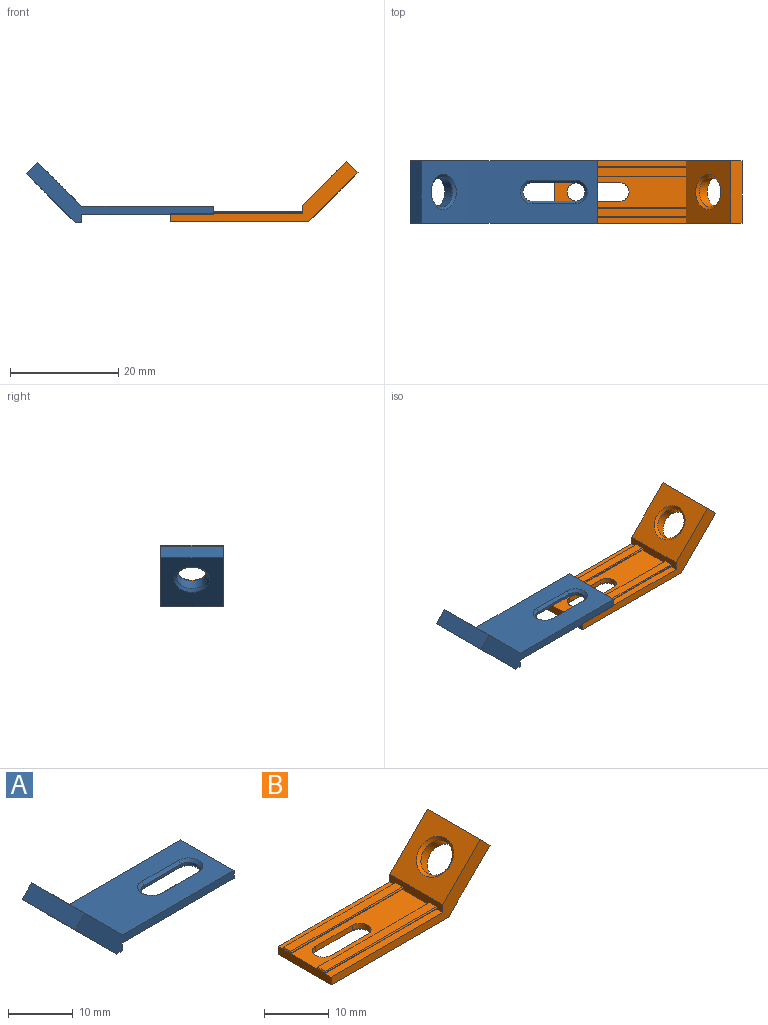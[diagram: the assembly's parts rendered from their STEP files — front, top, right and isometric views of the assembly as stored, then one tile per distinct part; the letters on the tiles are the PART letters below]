
ASSEMBLY  parts=2 mates=1
PART A: 41 faces, bbox 34.7x11.6x11.2 mm
  f0: plane 24.41x1.1mm, normal (0,0,-1), area 26.8mm2, adj f2,f5,f10,f21,f27
  f1: plane 24.41x5.6mm, normal (0,0,-1), area 86.2mm2, adj f2,f5,f16,f20,f25,f30,f31,f32
  f2: plane 11.6x1.5mm, normal (1,0,0), area 13mm2, adj f0,f1,f3,f4,f10,f11,f25,f26
  f3: plane 24.41x1.1mm, normal (0,0,-1), area 26.8mm2, adj f2,f5,f11,f17,f28
  f4: plane 24.41x11.6mm, normal (0,0,1), area 232.8mm2, adj f2,f6,f10,f11,f35,f36,f37,f38
  f5: plane 11.6x1.5mm, normal (1,0,0), area 17.4mm2, adj f0,f1,f3,f9,f10,f11,f19,f23
  f6: plane 11.6x8.2mm, normal (0.71,0,0.71), area 100.3mm2, adj f4,f7,f10,f11,f40
  f7: plane 11.6x2.12mm, normal (-0.71,0,0.71), area 34.8mm2, adj f6,f8,f10,f11
  f8: plane 11.6x9.08mm, normal (-0.71,0,-0.71), area 114.8mm2, adj f7,f9,f10,f11,f39
  f9: plane 11.6x1.24mm, normal (0,0,-1), area 14.4mm2, adj f5,f8,f10,f11
  f10: plane 34.73x11.2mm, normal (0,-1,0), area 75.1mm2, adj f0,f2,f4,f5,f6,f7,f8,f9
  f11: plane 34.73x11.2mm, normal (0,1,0), area 75.1mm2, adj f2,f3,f4,f5,f6,f7,f8,f9
  f12: plane 8x0.5mm, normal (0,1,0), area 4mm2, adj f13,f15,f31,f35
  f13: cylinder r=1.7mm len=3.4mm, axis (0,0,1), area 2.7mm2, adj f12,f14,f32,f37
  f14: plane 8x0.5mm, normal (0,-1,0), area 4mm2, adj f13,f15,f34,f38
  f15: cylinder r=1.7mm len=3.4mm, axis (0,0,1), area 2.7mm2, adj f12,f14,f33,f36
  f16: plane 24.45x0.5mm, normal (0,0.87,0.5), area 14mm2, adj f1,f18,f19,f30
  f17: plane 24.45x0.5mm, normal (0,-0.87,0.5), area 14mm2, adj f3,f18,f19,f28
  f18: plane 24.45x2.48mm, normal (0,0,-1), area 60.6mm2, adj f16,f17,f19,f29
  f19: plane 2.48x0.5mm, normal (0.87,0,0.5), area 1.3mm2, adj f5,f16,f17,f18
  f20: plane 24.45x0.5mm, normal (0,-0.87,0.5), area 14mm2, adj f1,f22,f23,f25
  f21: plane 24.45x0.5mm, normal (0,0.87,0.5), area 14mm2, adj f0,f22,f23,f27
  f22: plane 24.45x2.48mm, normal (0,0,-1), area 60.6mm2, adj f20,f21,f23,f26
  f23: plane 2.48x0.5mm, normal (0.87,0,0.5), area 1.3mm2, adj f5,f20,f21,f22
  f24: cylinder r=2.8mm len=5.6mm, axis (0.71,0,0.71), area 35.2mm2, adj f39,f40
  f25: plane 0.75x0.72mm, normal (0.71,-0.61,0.35), area 0.3mm2, adj f1,f2,f20,f26
  f26: plane 3.34x0.25mm, normal (0.71,0,-0.71), area 1mm2, adj f2,f22,f25,f27
  f27: plane 0.75x0.72mm, normal (0.71,0.61,0.35), area 0.3mm2, adj f0,f2,f21,f26
  f28: plane 0.75x0.72mm, normal (0.71,-0.61,0.35), area 0.3mm2, adj f2,f3,f17,f29
  f29: plane 3.34x0.25mm, normal (0.71,0,-0.71), area 1mm2, adj f2,f18,f28,f30
  f30: plane 0.75x0.72mm, normal (0.71,0.61,0.35), area 0.3mm2, adj f1,f2,f16,f29
  f31: plane 8x0.5mm, normal (0,0.71,-0.71), area 5.7mm2, adj f1,f12,f32,f33
  f32: cone r=2.2mm half-angle=45deg, axis (0,0,-1), area 4.3mm2, adj f1,f13,f31,f34
  f33: cone r=2.2mm half-angle=45deg, axis (0,0,-1), area 4.3mm2, adj f1,f15,f31,f34
  f34: plane 8x0.5mm, normal (0,-0.71,-0.71), area 5.7mm2, adj f1,f14,f32,f33
  f35: plane 8x0.5mm, normal (0,0.71,0.71), area 5.7mm2, adj f4,f12,f36,f37
  f36: cone r=2.2mm half-angle=45deg, axis (0,0,1), area 4.3mm2, adj f4,f15,f35,f38
  f37: cone r=2.2mm half-angle=45deg, axis (0,0,1), area 4.3mm2, adj f4,f13,f35,f38
  f38: plane 8x0.5mm, normal (0,-0.71,0.71), area 5.7mm2, adj f4,f14,f36,f37
  f39: cone r=2.8mm half-angle=45deg, axis (-0.71,0,-0.71), area 13.6mm2, adj f8,f24
  f40: cone r=2.8mm half-angle=45deg, axis (0.71,0,0.71), area 13.6mm2, adj f6,f24
PART B: 44 faces, bbox 34.9x11.6x11.2 mm
  f0: plane 24.41x6.25mm, normal (0,0,1), area 110.2mm2, adj f4,f8,f11,f12,f13,f14,f17,f19
  f1: plane 24.41x1.43mm, normal (0,0,1), area 31.7mm2, adj f4,f8,f10,f15,f24
  f2: plane 24.41x1.43mm, normal (0,0,1), area 31.7mm2, adj f4,f8,f9,f21,f32
  f3: plane 25.65x11.6mm, normal (0,0,-1), area 247.2mm2, adj f4,f5,f9,f10,f38,f39,f40,f41
  f4: plane 11.6x1.5mm, normal (-1,0,0), area 17.4mm2, adj f0,f1,f2,f3,f9,f10,f16,f20
  f5: plane 11.6x9.08mm, normal (0.71,0,-0.71), area 114.8mm2, adj f3,f6,f9,f10,f42
  f6: plane 11.6x2.12mm, normal (0.71,0,0.71), area 34.8mm2, adj f5,f7,f9,f10
  f7: plane 11.6x8.2mm, normal (-0.71,0,0.71), area 100.3mm2, adj f6,f8,f9,f10,f43
  f8: plane 11.6x1.5mm, normal (-1,0,0), area 15.7mm2, adj f0,f1,f2,f7,f9,f10,f15,f17
  f9: plane 34.73x11.2mm, normal (0,-1,0), area 75.1mm2, adj f2,f3,f4,f5,f6,f7,f8
  f10: plane 34.73x11.2mm, normal (0,1,0), area 75.1mm2, adj f1,f3,f4,f5,f6,f7,f8
  f11: plane 8x1mm, normal (0,1,0), area 8mm2, adj f0,f12,f14,f38
  f12: cylinder r=1.7mm len=3.4mm, axis (0,0,1), area 5.3mm2, adj f0,f11,f13,f39
  f13: plane 8x1mm, normal (0,-1,0), area 8mm2, adj f0,f12,f14,f41
  f14: cylinder r=1.7mm len=3.4mm, axis (0,0,1), area 5.3mm2, adj f0,f11,f13,f40
  f15: plane 24.45x0.28mm, normal (0,0.87,-0.5), area 8mm2, adj f1,f8,f24,f25
  f16: plane 1.58x0.28mm, normal (-0.87,0,-0.5), area 0.5mm2, adj f4,f24,f27,f28
  f17: plane 24.45x0.28mm, normal (0,-0.87,-0.5), area 8mm2, adj f0,f8,f27,f30
  f18: plane 24.45x1.58mm, normal (0,0,1), area 38.6mm2, adj f8,f25,f28,f30
  f19: plane 24.45x0.28mm, normal (0,0.87,-0.5), area 8mm2, adj f0,f8,f35,f37
  f20: plane 1.58x0.28mm, normal (-0.87,0,-0.5), area 0.5mm2, adj f4,f32,f34,f35
  f21: plane 24.45x0.28mm, normal (0,-0.87,-0.5), area 8mm2, adj f2,f8,f31,f32
  f22: plane 24.45x1.58mm, normal (0,0,1), area 38.6mm2, adj f8,f31,f34,f37
  f23: cylinder r=2.8mm len=5.6mm, axis (-0.71,0,0.71), area 35.2mm2, adj f42,f43
  f24: plane 0.29x0.29mm, normal (-0.55,0.55,-0.63), area 0.1mm2, adj f1,f15,f16,f26
  f25: plane 24.45x0.22mm, normal (0,0.87,0.5), area 6.1mm2, adj f8,f15,f18,f26
  f26: plane 0.22x0.13mm, normal (-0.65,0.65,0.38), area 0mm2, adj f24,f25,f28
  f27: plane 0.29x0.29mm, normal (-0.55,-0.55,-0.63), area 0.1mm2, adj f0,f16,f17,f29
  f28: plane 1.58x0.22mm, normal (-0.87,0,0.5), area 0.4mm2, adj f16,f18,f26,f29
  f29: plane 0.22x0.13mm, normal (-0.65,-0.65,0.38), area 0mm2, adj f27,f28,f30
  f30: plane 24.45x0.22mm, normal (0,-0.87,0.5), area 6.1mm2, adj f8,f17,f18,f29
  f31: plane 24.45x0.22mm, normal (0,-0.87,0.5), area 6.1mm2, adj f8,f21,f22,f33
  f32: plane 0.29x0.29mm, normal (-0.55,-0.55,-0.63), area 0.1mm2, adj f2,f20,f21,f33
  f33: plane 0.22x0.13mm, normal (-0.65,-0.65,0.38), area 0mm2, adj f31,f32,f34
  f34: plane 1.58x0.22mm, normal (-0.87,0,0.5), area 0.4mm2, adj f20,f22,f33,f36
  f35: plane 0.29x0.29mm, normal (-0.55,0.55,-0.63), area 0.1mm2, adj f0,f19,f20,f36
  f36: plane 0.22x0.13mm, normal (-0.65,0.65,0.38), area 0mm2, adj f34,f35,f37
  f37: plane 24.45x0.22mm, normal (0,0.87,0.5), area 6.1mm2, adj f8,f19,f22,f36
  f38: plane 8x0.5mm, normal (0,0.71,-0.71), area 5.7mm2, adj f3,f11,f39,f40
  f39: cone r=2.2mm half-angle=45deg, axis (0,0,-1), area 4.3mm2, adj f3,f12,f38,f41
  f40: cone r=2.2mm half-angle=45deg, axis (0,0,-1), area 4.3mm2, adj f3,f14,f38,f41
  f41: plane 8x0.5mm, normal (0,-0.71,-0.71), area 5.7mm2, adj f3,f13,f39,f40
  f42: cone r=3.3mm half-angle=45deg, axis (0.71,0,-0.71), area 13.6mm2, adj f5,f23
  f43: cone r=2.8mm half-angle=45deg, axis (-0.71,0,0.71), area 13.6mm2, adj f7,f23
PLACE A t=(-49.49,14.14,-12.57)mm
PLACE B t=(-41.29,14.14,-12.45)mm
MATE slider A.f2 <-> B.f4  axis (1,0,0) through (-41.36,2.54,-7.49)mm
